# Revit family: Flushometer-Toilet_Touchless-KOHLER-Mach_Wave-K-40TH00K10
name_source: partatom
category: Plumbing Fixtures
units: mm (PartAtom-declared; Revit-internal decimal feet)

## family parameters
Cut with Voids When Loaded = No
Host = Face
OmniClass Number = 23.27.31.00
OmniClass Title = Valves
Part Type = Normal
Room Calculation Point = No
Round Connector Dimension = Use Diameter
Shared = No

## types (1)
- CP-Polished Chrome
    ADA Compliant = Yes
    Assembly Code = D2020
    CW Connection = Yes
    Cold Water Inlet = Cold Water Inlet
    Cold Water Outlet = Cold Water Outlet
    Date Modified = 04/28/2023
    Default Elevation = 36"
    Description = Touchless toilet flushometer, HES-powered, 1.0 gpf
    Finish = Kohler-Metal-CP-Polished_Chrome
    Flow Rate = 25 GPM
    Flush Rate- GPF = 1.0 GPF
    Flush Rate- LPF = 3.8 LPF
    HW Connection = No
    Hot Water Inlet = Hot Water Inlet
    Manufacturer = Kohler Co.
    Master Format 2014 = 23 09 13.33
    Master Format 2014 Name = Control Valves
    Material = Premium Metal Construction
    Model = K-40TH00K10-CP
    Pressure = 80.00 psi
    Product Documentation Link = https://www.us.kohler.com
    Product Name = Mach Wave
    Product Page URL = http://www.us.kohler.com
    Type = 1
    URL = https://www.us.kohler.com
    Vent Connection = No
    Waste Connection = No
    Waste Water Outlet = Waste Water Outlet
    WaterSense Certified = Yes

## geometry (parser evidence)
native form markers: Sweep x6
no freeform markers — native parametric forms only
